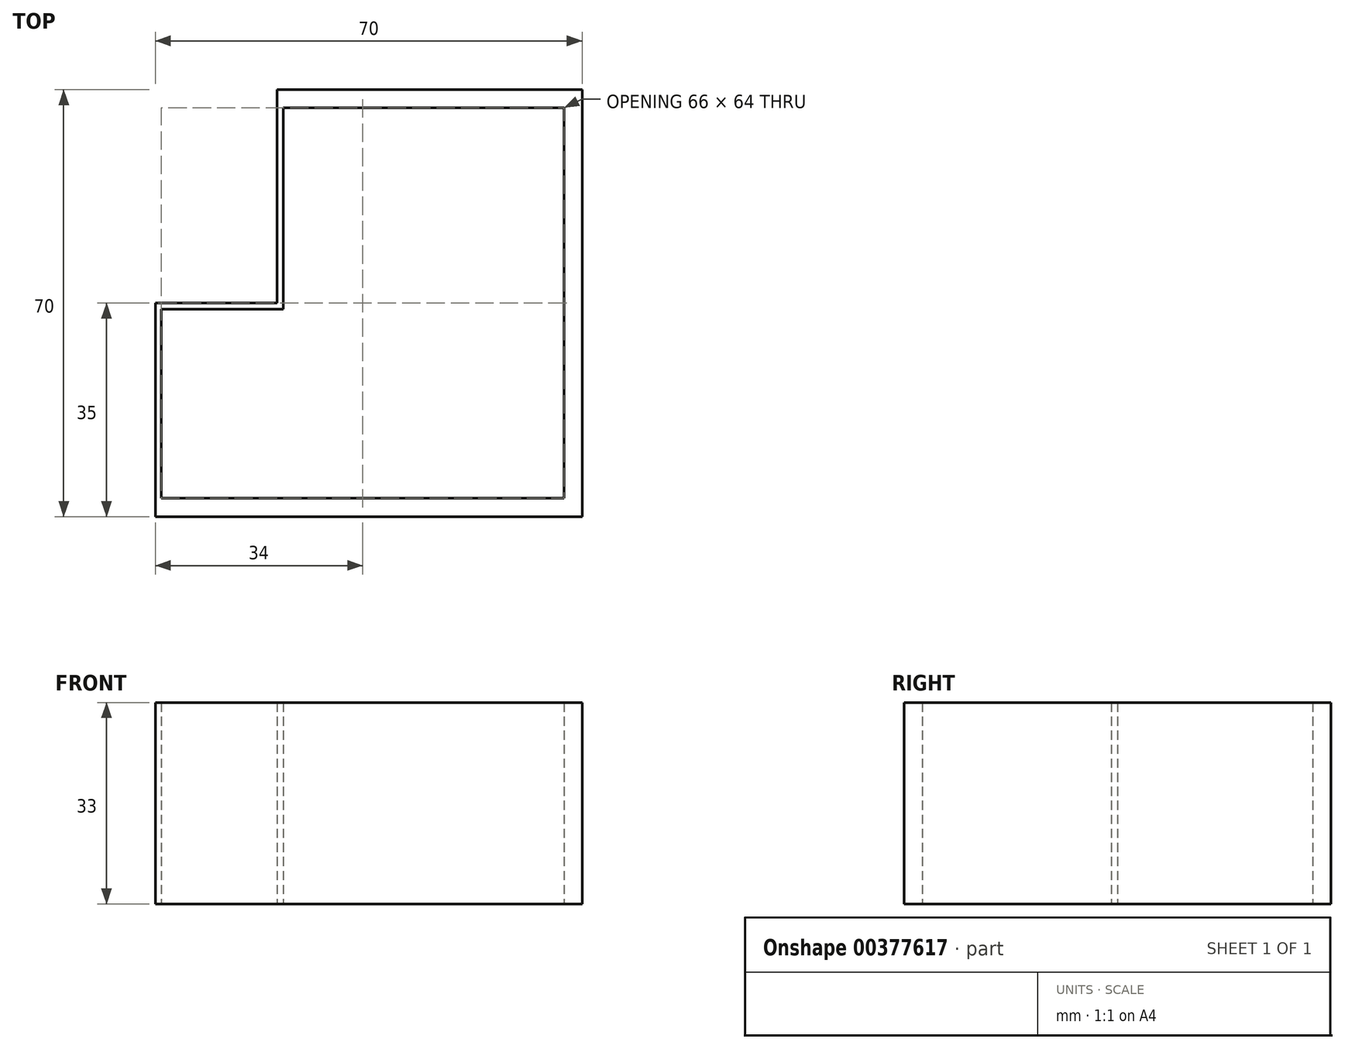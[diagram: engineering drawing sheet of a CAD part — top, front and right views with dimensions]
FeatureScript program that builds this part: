
annotation { "Feature Type Name" : "Feature", "Feature Type Description" : "" }
export const myFeature = defineFeature(function(context is Context, id is Id, definition is map)
    precondition{}
    {
        {
            var Q0;
            Q0=qCreatedBy(makeId("Top.planeOp"),FACE);
            var sketch = newSketch(context, id + "F0", { "sketchPlane" : qUnion([Q0])});
            skLineSegment(sketch, "E0", {"start": v(0, 0) * mm, "end": v(70, 0) * mm});
            skLineSegment(sketch, "E1", {"start": v(70, 0) * mm, "end": v(70, 70) * mm});
            skLineSegment(sketch, "E2", {"start": v(70, 70) * mm, "end": v(20, 70) * mm});
            skLineSegment(sketch, "E3", {"start": v(20, 70) * mm, "end": v(20, 35) * mm});
            skLineSegment(sketch, "E4", {"start": v(20, 35) * mm, "end": v(0, 35) * mm});
            skLineSegment(sketch, "E5", {"start": v(0, 35) * mm, "end": v(0, 0) * mm});
            skLineSegment(sketch, "E6", {"start": v(0, 0) * mm, "end": v(3, 0) * mm});
            skLineSegment(sketch, "E7", {"start": v(3, 0) * mm, "end": v(3, 3) * mm});
            skLineSegment(sketch, "E8", {"start": v(3, 3) * mm, "end": v(67, 3) * mm});
            skLineSegment(sketch, "E9", {"start": v(67, 3) * mm, "end": v(67, 67) * mm});
            skLineSegment(sketch, "E10", {"start": v(67, 67) * mm, "end": v(21, 67) * mm});
            skLineSegment(sketch, "E11", {"start": v(21, 67) * mm, "end": v(21, 34) * mm});
            skLineSegment(sketch, "E12", {"start": v(21, 34) * mm, "end": v(1, 34) * mm});
            skLineSegment(sketch, "E13", {"start": v(1, 34) * mm, "end": v(1, 3) * mm});
            skLineSegment(sketch, "E14", {"start": v(1, 3) * mm, "end": v(3, 3) * mm});
            skSolve(sketch);
        }
        {
            var Q0;
            Q0=makeQuery(id+"F0.imprint","IMPRINT",FACE,{"disambiguationData":[TD([[makeQuery(id+"F0.imprint","IMPRINT",EDGE,{"derivedFrom":sQuery(id+"F0.wireOp",EDGE,"E0")}),1.0]])]});
            extrude(context, id + "F1", {"entities" : qUnion([Q0]), "depth" : 30 * mm, "hasSecondDirection" : true, "secondDirectionOppositeDirection" : true, "secondDirectionDepth" : 3 * mm});
        }
    });
